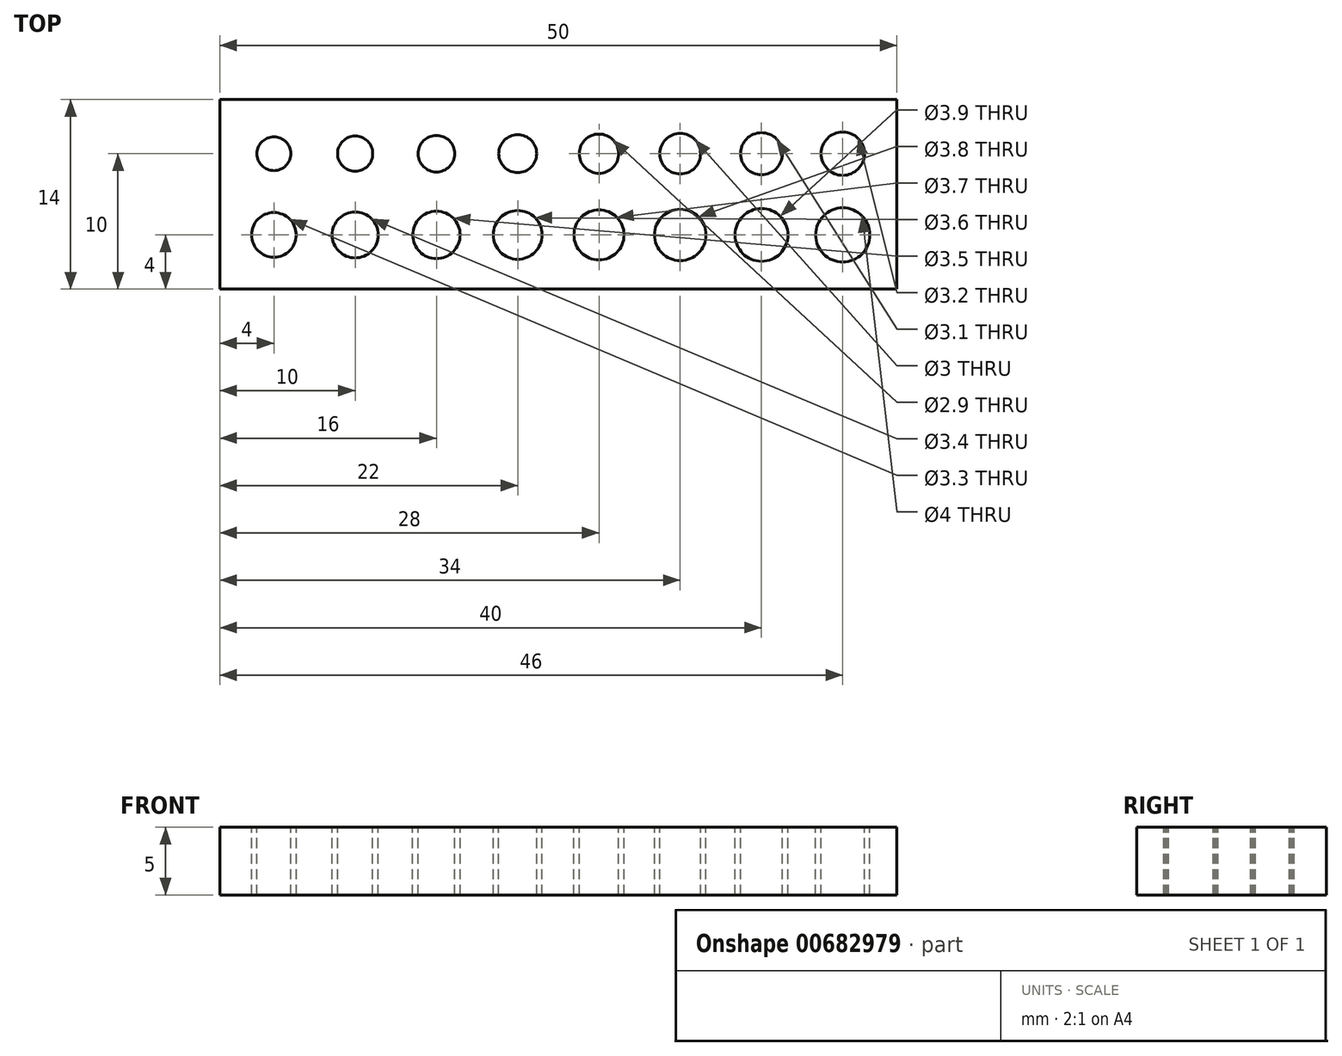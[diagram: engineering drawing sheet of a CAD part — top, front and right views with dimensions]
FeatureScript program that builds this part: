
annotation { "Feature Type Name" : "Feature", "Feature Type Description" : "" }
export const myFeature = defineFeature(function(context is Context, id is Id, definition is map)
    precondition{}
    {
        {
            var Q0;
            Q0=qCreatedBy(makeId("Top.planeOp"),FACE);
            var sketch = newSketch(context, id + "F0", { "sketchPlane" : qUnion([Q0])});
            skLineSegment(sketch, "E0.bottom", {"start": v(25, 7) * mm, "end": v(-25, 7) * mm});
            skLineSegment(sketch, "E0.top", {"start": v(25, -7) * mm, "end": v(-25, -7) * mm});
            skLineSegment(sketch, "E0.left", {"start": v(25, 7) * mm, "end": v(25, -7) * mm});
            skLineSegment(sketch, "E0.right", {"start": v(-25, 7) * mm, "end": v(-25, -7) * mm});
            skPoint(sketch, "E0.middle", {"position": v(0, 0) * mm});
            skLineSegment(sketch, "E1", {"start": v(-25, 3) * mm, "end": v(25, 3) * mm, "construction": true});
            skLineSegment(sketch, "E2", {"start": v(-25, -3) * mm, "end": v(25, -3) * mm, "construction": true});
            skLineSegment(sketch, "E3", {"start": v(-21, -7) * mm, "end": v(-21, 7) * mm, "construction": true});
            skLineSegment(sketch, "E4", {"start": v(-15, -7) * mm, "end": v(-15, 7) * mm, "construction": true});
            skLineSegment(sketch, "E5", {"start": v(-9, -7) * mm, "end": v(-9, 7) * mm, "construction": true});
            skLineSegment(sketch, "E6", {"start": v(-3, -7) * mm, "end": v(-3, 7) * mm, "construction": true});
            skLineSegment(sketch, "E7.MirrorCS", {"start": v(3, -7) * mm, "end": v(3, 7) * mm, "construction": true});
            skLineSegment(sketch, "E8.MirrorCS", {"start": v(9, -7) * mm, "end": v(9, 7) * mm, "construction": true});
            skLineSegment(sketch, "E9.MirrorCS", {"start": v(15, -7) * mm, "end": v(15, 7) * mm, "construction": true});
            skLineSegment(sketch, "E10.MirrorCS", {"start": v(21, -7) * mm, "end": v(21, 7) * mm, "construction": true});
            skCircle(sketch, "E11", {"center": v(-21, 3) * mm, "radius": 1.25 * mm});
            skCircle(sketch, "E12", {"center": v(-21, -3) * mm, "radius": 1.65 * mm});
            skCircle(sketch, "E13", {"center": v(-15, 3) * mm, "radius": 1.3 * mm});
            skCircle(sketch, "E14", {"center": v(-15, -3) * mm, "radius": 1.7 * mm});
            skCircle(sketch, "E15", {"center": v(-9, 3) * mm, "radius": 1.35 * mm});
            skCircle(sketch, "E16", {"center": v(-3, 3) * mm, "radius": 1.4 * mm});
            skCircle(sketch, "E17", {"center": v(3, 3) * mm, "radius": 1.45 * mm});
            skCircle(sketch, "E18", {"center": v(9, 3) * mm, "radius": 1.5 * mm});
            skCircle(sketch, "E19", {"center": v(15, 3) * mm, "radius": 1.55 * mm});
            skCircle(sketch, "E20", {"center": v(21, 3) * mm, "radius": 1.6 * mm});
            skCircle(sketch, "E21", {"center": v(-9, -3) * mm, "radius": 1.75 * mm});
            skCircle(sketch, "E22", {"center": v(-3, -3) * mm, "radius": 1.8 * mm});
            skCircle(sketch, "E23", {"center": v(3, -3) * mm, "radius": 1.85 * mm});
            skCircle(sketch, "E24", {"center": v(9, -3) * mm, "radius": 1.9 * mm});
            skCircle(sketch, "E25", {"center": v(15, -3) * mm, "radius": 1.95 * mm});
            skCircle(sketch, "E26", {"center": v(21, -3) * mm, "radius": 2 * mm});
            skSolve(sketch);
        }
        {
            var Q0;
            Q0 = qSketchRegion(id + "F0", true);
            extrude(context, id + "F1", {"entities" : qUnion([Q0]), "oppositeDirection" : true, "depth" : 5 * mm, "offsetDistance" : 25 * mm});
        }
    });
